# Revit family: 1702a_OPE
name_source: partatom
category: Communication Devices
units: mm (PartAtom-declared; Revit-internal decimal feet)

## family parameters
Cut with Voids When Loaded = No
Host = Face
Maintain Annotation Orientation = No
OmniClass Number = 23.85.80.11.27
OmniClass Title = Lighting Controls
Part Type = Normal
Room Calculation Point = No
Round Connector Dimension = Use Diameter
Shared = Yes

## types (1)
- 1702a_OPE
    Assembly Code = D5090
    Certifications = UL and cUL listed
    Default Elevation = 48 "
    Description = The OPE is a NEMA Type 4X enclosure specifically designed for use with HCS’s OMNIIR ceiling mount occupancy sensor. Designed to provide protection from foreign materials and water, the enclosure is acceptable for use in a variety of environments including applications in the pharmaceutical and food
pre-paration industries
    Glass = Glass - White
    Height = 6.5 "
    Housing Material = Paint -  Matte White
    Manufacturer = NX Lighting Controls
    Model = OPE – OMNI Protective Enclosure
    Type Comments = OPE – OMNI Protective Enclosure
    URL = https://www.currentlighting.com
    Warranty = 5-Years Warranty
    Width = 6.5 "

## geometry (parser evidence)
native form markers: Sweep x3
no freeform markers — native parametric forms only
